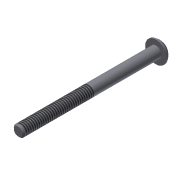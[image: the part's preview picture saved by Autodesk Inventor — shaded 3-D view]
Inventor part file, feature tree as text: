
AUTODESK INVENTOR PART (.ipt)
format: ipt  version: 2013 (Build 170138000, 138)  size: 121,344 bytes
history: native  units: in
note: dims shown in document units (in); Inventor stores cm internally (conversion verified against a paired STEP export)
features: sketch x3, extrude x2, revolve x1, chamfer x1, thread x1
ambient origin geometry x8: Origin, YZ Plane, XZ Plane, XY Plane, X Axis, Y Axis, Z Axis, Center Point
bodies: Solid1 (feature_tree)
feature tree (8):
  extrude  "Extrusion1"  Depth=2.0in TaperAngle=0.0deg
  revolve  "Revolution1"  [1 undecoded]
  extrude  "Extrusion2"  Depth=0.0938in
  chamfer  "Chamfer1"  Distance=0.0625in
  thread  "Thread1"  [1 undecoded]
  sketch  "Sketch1"  dims[d0=0.164in d1=2.0in d2=0.0in]
  sketch  "Sketch2"  dims[d3=0.087in d6=0.08in]
  sketch  "Sketch3"  dims[d7=90.0deg d8=0.0938in d9=0.0625in d10=0.0in d13=0.02in d14=0.125in d15=45.0deg d16=1.0in d17=0.0in d19=0.156in]
note: 2 required parameter values undecoded (feature->parameter linkage not recoverable at this tier; creation-order binding heuristic only, values carry confidence <= 0.55)